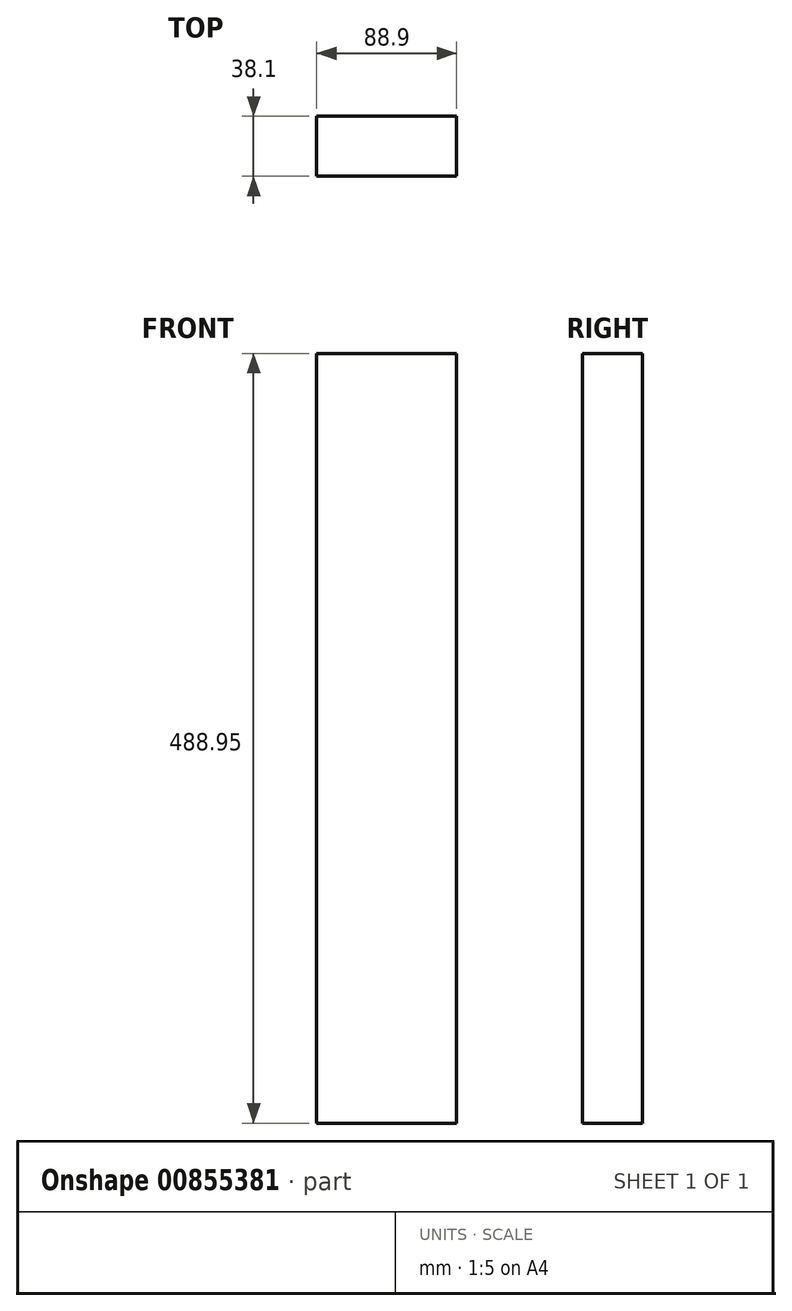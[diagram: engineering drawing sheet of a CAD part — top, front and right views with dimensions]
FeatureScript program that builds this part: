
annotation { "Feature Type Name" : "Feature", "Feature Type Description" : "" }
export const myFeature = defineFeature(function(context is Context, id is Id, definition is map)
    precondition{}
    {
        {
            var Q0;
            Q0=qCreatedBy(makeId("Top.planeOp"),FACE);
            var sketch = newSketch(context, id + "F0", { "sketchPlane" : qUnion([Q0])});
            skLineSegment(sketch, "E0.bottom", {"start": v(0, 0) * mm, "end": v(88.9, 0) * mm});
            skLineSegment(sketch, "E0.top", {"start": v(0, 38.1) * mm, "end": v(88.9, 38.1) * mm});
            skLineSegment(sketch, "E0.left", {"start": v(0, 0) * mm, "end": v(0, 38.1) * mm});
            skLineSegment(sketch, "E0.right", {"start": v(88.9, 0) * mm, "end": v(88.9, 38.1) * mm});
            skSolve(sketch);
        }
        {
            var Q0;
            Q0 = qSketchRegion(id + "F0", true);
            extrude(context, id + "F1", {"entities" : qUnion([Q0]), "depth" : 488.95 * mm, "offsetDistance" : 25.4 * mm});
        }
    });
